# Revit family: BE_84253_de_DE
name_source: partatom
category: Leuchten
units: mm (PartAtom-declared; Revit-internal decimal feet)

## family parameters
Basisbauteil = Fläche
Beim Laden mit Abzugskörper schneiden = Ja
Bemaßung runder Anschluss = Durchmesser verwenden
Gemeinsam genutzt = Nein
Lichtquelle = Nein
Raumberechnungspunkt = Ja
Teiletyp = Normal

## types (4) — shared parameters
AC/DC = AC/DC
Aktualisierung = 2022-09-22T04:00:02
Anschlussleitung = 6.0 m X05BQ-F 4 × 1 mm²
Beschreibung = Aufsatzleuchte
Beschreibung_Sonderanfertigung = Hier können Sie Informationen zur Sonderanfertigung eintragen.
CE_Konformität = ja
ENEC = ja
Energieeffizienzklasse = LED A++ - A
Farbwiedergabeindex = CRI > 80
Frequenz = 0/50-60 Hz
Gewicht = 9.3 kg
Hersteller = BEGA
Lampe = LED 25.2 W
Lastklassifizierung = Beleuchtung
Lebensdauerkriterien = L70B50 @ 25 °C = 200000 h
Logo = BEGA_Logo.png
Material_02 = BEGA_Oberfläche_Silber_matt
Material_03 = BEGA_Oberfläche_Weiss_matt
Material_06 = BEGA_Oberfläche_Edelstahl_gebürstet
Material_09 = BEGA_Glas_klar
Material_11 = BEGA_Glas_opal
Material_15 = BEGA_Leuchtmedium_matt
Material_17 = BEGA_Reflektor
Material_18 = BEGA_Gummi_schwarz
Produktdatenblatt = https://cdn.bega.com
Scheinlast = 0 VA
Schutzart = IP 66
Schutzklasse = II
Sonderanfertigung = Nein
Spannung = 240 V
Typenbild = 84253.png
URL = https://www.bega.com
Umgebungstemperatur = 25 °C
zero-valued in all types: Vorgabe-Ansicht

## per-type parameters (varying)
| type | BEGA_IES1 | BEGA_IES2 | Bestellnummer | Farbtemperatur | LED_Modulbezeichnung | Lampenlichtstrom | Leuchtenlichtstrom | M_A | M_G | Modell |
| BEGA_84253_Silber_K3 | Ja | Nein | 84253AK3 | 3000 K | 2x LED-0970/830 | 4890 lm | 4019 lm | Ja | Nein | 84253AK3 |
| BEGA_84253_Silber_K4 | Nein | Ja | 84253AK4 | 4000 K | 2x LED-0970/840 | 5020 lm | 4126 lm | Ja | Nein | 84253AK4 |
| BEGA_84253_Grafit_K4 | Nein | Ja | 84253K4 | 4000 K | 2x LED-0970/840 | 5020 lm | 4126 lm | Nein | Ja | 84253K4 |
| BEGA_84253_Grafit_K3 | Ja | Nein | 84253K3 | 3000 K | 2x LED-0970/830 | 4890 lm | 4019 lm | Nein | Ja | 84253K3 |

## geometry (parser evidence)
native form markers: Blend x2, Sweep x29
no freeform markers — native parametric forms only
